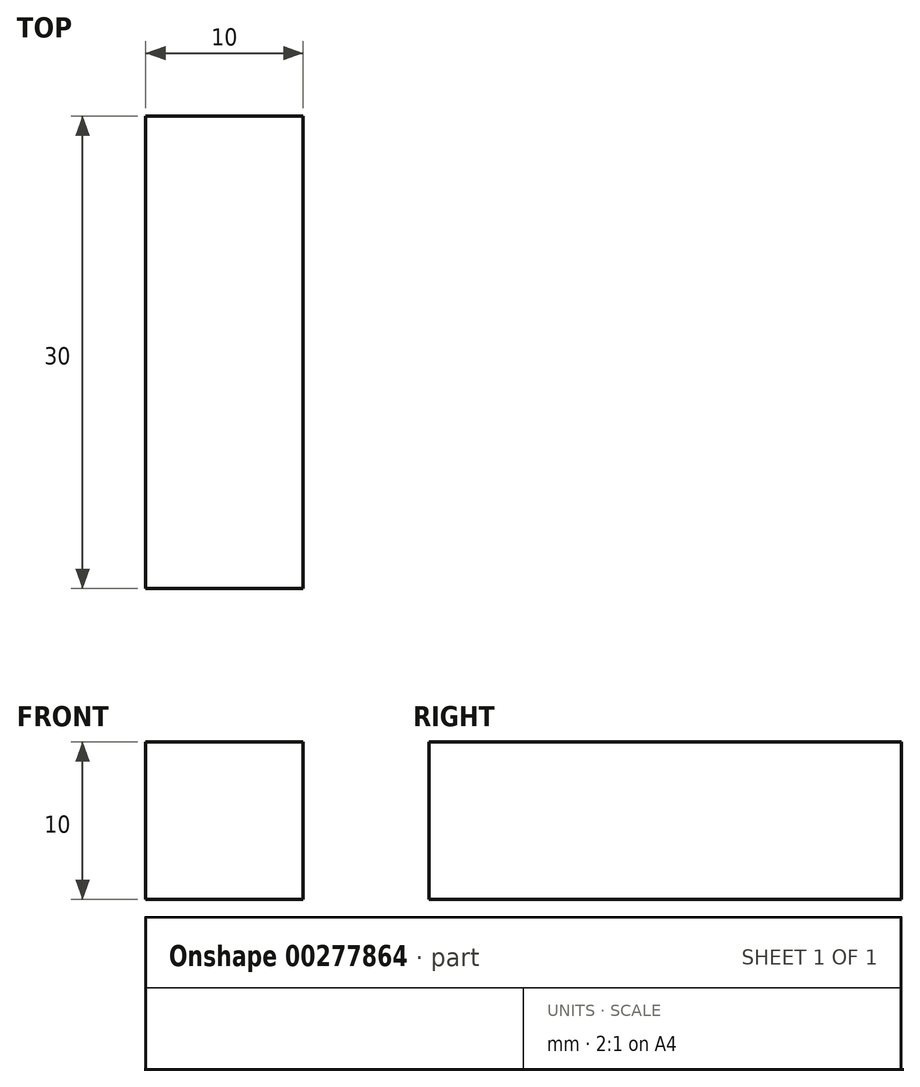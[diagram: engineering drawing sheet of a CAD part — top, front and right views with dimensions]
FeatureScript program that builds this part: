
annotation { "Feature Type Name" : "Feature", "Feature Type Description" : "" }
export const myFeature = defineFeature(function(context is Context, id is Id, definition is map)
    precondition{}
    {
        {
            var Q0;
            Q0=qCreatedBy(makeId("Front.planeOp"),FACE);
            var sketch = newSketch(context, id + "F0", { "sketchPlane" : qUnion([Q0])});
            skLineSegment(sketch, "E0.bottom", {"start": v(0, 0) * mm, "end": v(30, 0) * mm});
            skLineSegment(sketch, "E0.top", {"start": v(0, 30) * mm, "end": v(30, 30) * mm});
            skLineSegment(sketch, "E0.left", {"start": v(0, 0) * mm, "end": v(0, 30) * mm});
            skLineSegment(sketch, "E0.right", {"start": v(30, 0) * mm, "end": v(30, 30) * mm});
            skLineSegment(sketch, "E1.bottom", {"start": v(0, 0) * mm, "end": v(10, 0) * mm});
            skLineSegment(sketch, "E1.top", {"start": v(0, 10) * mm, "end": v(10, 10) * mm});
            skLineSegment(sketch, "E1.left", {"start": v(0, 0) * mm, "end": v(0, 10) * mm});
            skLineSegment(sketch, "E1.right", {"start": v(10, 0) * mm, "end": v(10, 10) * mm});
            skLineSegment(sketch, "E2", {"start": v(10, 30) * mm, "end": v(30, 10) * mm});
            skSolve(sketch);
        }
        {
            var Q0;
            {var subQ1=sQuery(id+"F0.wireOp",EDGE,"E0.bottom");Q0=makeQuery(id+"F0.imprint","IMPRINT",FACE,{"disambiguationData":[TD([[makeQuery(id+"F0.imprint","IMPRINT",EDGE,{"derivedFrom":subQ1}),1.0]])]});}
            extrude(context, id + "F1", {"entities" : qUnion([Q0]), "depth" : 30 * mm});
        }
        {
            var Q0;
            Q0=makeQuery(id+"F1.opExtrude","SWEPT_FACE",FACE,{"disambiguationData":[OSD([sQuery(id+"F0.wireOp",EDGE,"E0.bottom")])]});
            var sketch = newSketch(context, id + "F2", { "sketchPlane" : qUnion([Q0])});
            skLineSegment(sketch, "E3.bottom", {"start": v(30, 20) * mm, "end": v(20, 20) * mm});
            skLineSegment(sketch, "E3.top", {"start": v(30, 10) * mm, "end": v(20, 10) * mm});
            skLineSegment(sketch, "E3.left", {"start": v(30, 20) * mm, "end": v(30, 10) * mm});
            skLineSegment(sketch, "E3.right", {"start": v(20, 20) * mm, "end": v(20, 10) * mm});
            skSolve(sketch);
        }
        {
            var Q0;
            Q0 = qSketchRegion(id + "F2", true);
            extrude(context, id + "F3", {"entities" : qUnion([Q0]), "operationType" : NewBodyOperationType.REMOVE, "endBound" : BoundingType.THROUGH_ALL, "oppositeDirection" : true, "depth" : 25 * mm});
        }
    });
